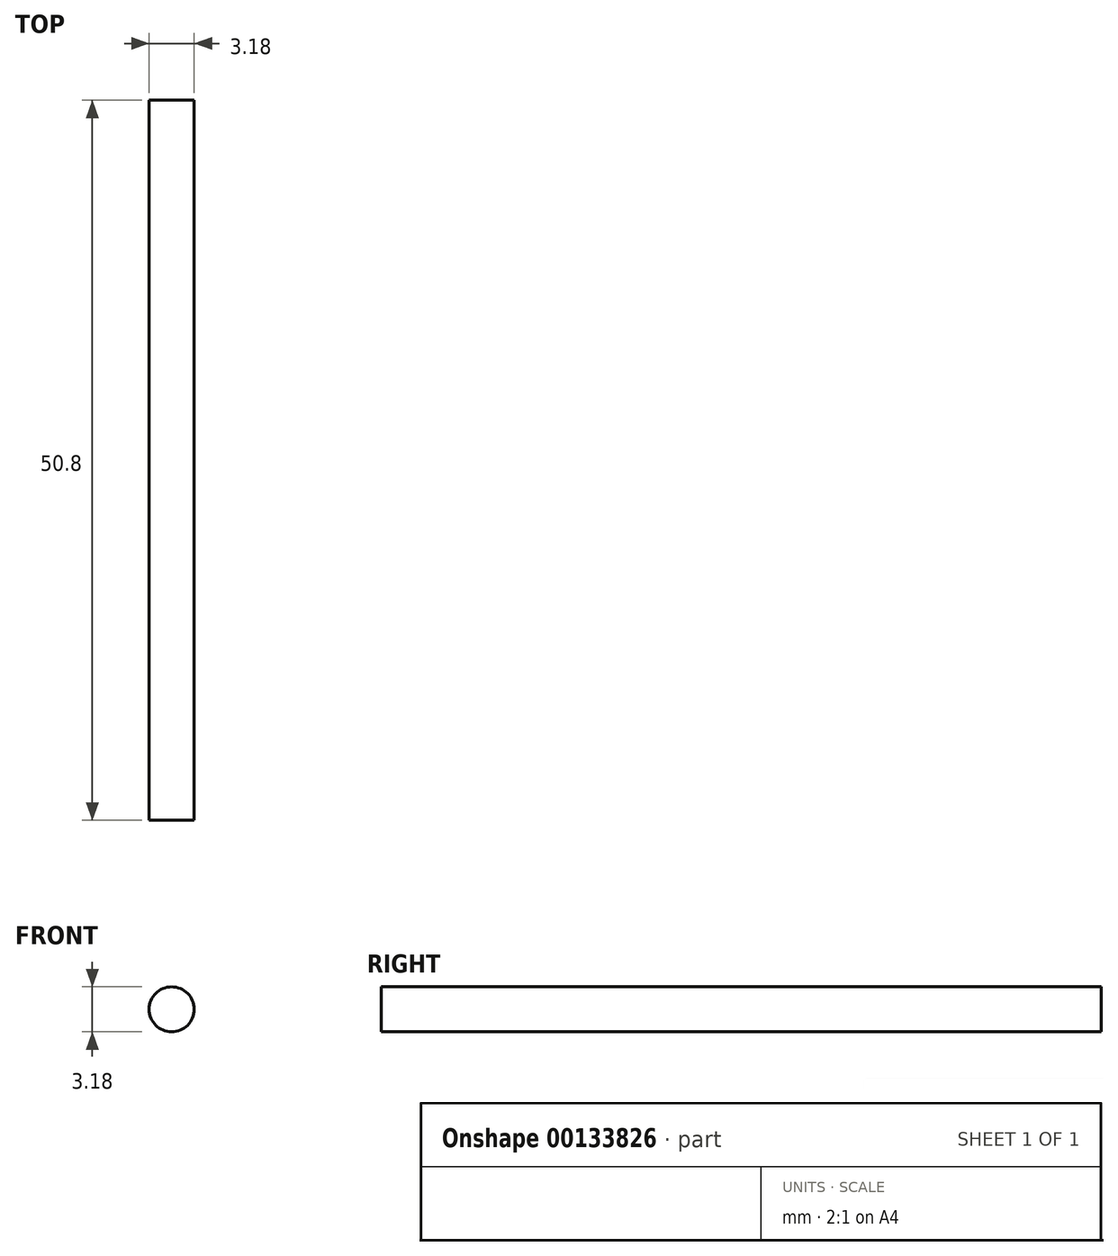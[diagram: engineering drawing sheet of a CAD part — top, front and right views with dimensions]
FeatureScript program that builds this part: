
annotation { "Feature Type Name" : "Feature", "Feature Type Description" : "" }
export const myFeature = defineFeature(function(context is Context, id is Id, definition is map)
    precondition{}
    {
        {
            var Q0;
            Q0=qCreatedBy(makeId("Top.planeOp"),FACE);
            var sketch = newSketch(context, id + "F0", { "sketchPlane" : qUnion([Q0])});
            skLineSegment(sketch, "E0.bottom", {"start": v(-110.62, 19.73) * mm, "end": v(-109.03, 19.73) * mm});
            skLineSegment(sketch, "E0.top", {"start": v(-110.62, -31.07) * mm, "end": v(-109.03, -31.07) * mm});
            skLineSegment(sketch, "E0.left", {"start": v(-110.62, 19.73) * mm, "end": v(-110.62, -31.07) * mm});
            skLineSegment(sketch, "E0.right", {"start": v(-109.03, 19.73) * mm, "end": v(-109.03, -31.07) * mm});
            skSolve(sketch);
        }
        {
            var Q0;
            Q0=makeQuery(id+"F0.imprint","IMPRINT",FACE,{"disambiguationData":[TD([[makeQuery(id+"F0.imprint","IMPRINT",EDGE,{"derivedFrom":sQuery(id+"F0.wireOp",EDGE,"E0.bottom")}),-1.0]])]});
            var Q1;
            Q1=sQuery(id+"F0.wireOp",EDGE,"E0.left");
            revolve(context, id + "F1", {"entities" : qUnion([Q0]), "axis" : qUnion([Q1]), "revolveType" : RevolveType.FULL});
        }
    });
